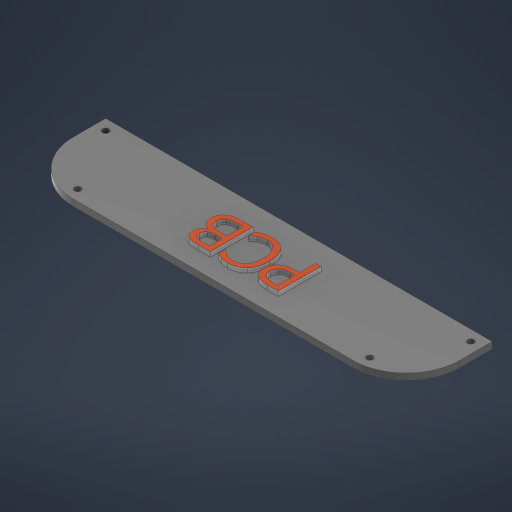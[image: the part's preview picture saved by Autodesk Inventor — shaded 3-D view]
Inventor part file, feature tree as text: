
AUTODESK INVENTOR PART (.ipt)
format: ipt  version: 2024 (Build 280153000, 153)  size: 323,584 bytes
history: native  units: mm
features: other x4, extrude x2, sketch x2
ambient origin geometry x8: Origin, YZ Plane, XZ Plane, XY Plane, X Axis, Y Axis, Z Axis, Center Point
bodies: Body1 (feature_tree)
feature tree (8):
  other  "솔리드1"
  extrude  "돌출1"  Depth=180.0mm
  extrude  "돌출2"  Depth=40.0mm
  sketch  "스케치1"
  sketch  "스케치2"
  other  "Finish1"
  other  "Finish2"
  other  "Finish3"
